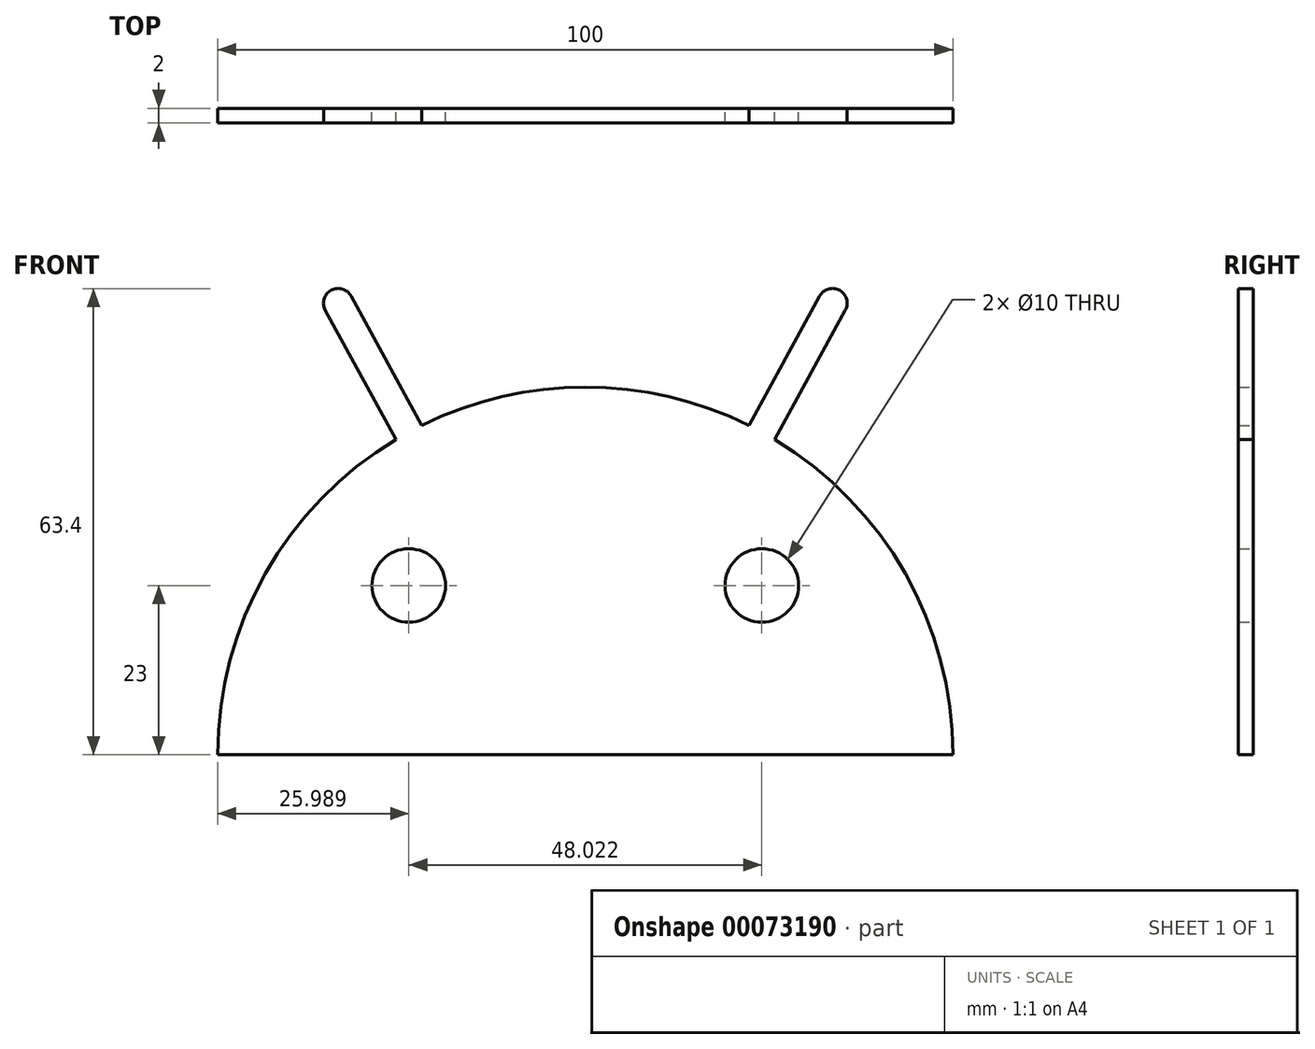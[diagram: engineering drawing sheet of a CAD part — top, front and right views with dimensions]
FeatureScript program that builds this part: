
annotation { "Feature Type Name" : "Feature", "Feature Type Description" : "" }
export const myFeature = defineFeature(function(context is Context, id is Id, definition is map)
    precondition{}
    {
        {
            var Q0;
            Q0=qCreatedBy(makeId("Front.planeOp"),FACE);
            var sketch = newSketch(context, id + "F0", { "sketchPlane" : qUnion([Q0])});
            skLineSegment(sketch, "E0", {"start": v(-50, 0) * mm, "end": v(50, 0) * mm});
            skArc(sketch, "E1", {"start": v(50, 0) * mm, "mid": v(0, 50) * mm, "end": v(-50, 0) * mm});
            skLineSegment(sketch, "E2", {"start": v(0, 0) * mm, "end": v(38.37, 70.1) * mm, "construction": true});
            skPoint(sketch, "E3", {"position": v(24.01, 43.86) * mm});
            skPoint(sketch, "E4", {"position": v(25.75, 42.86) * mm});
            skLineSegment(sketch, "E5", {"start": v(25.75, 42.86) * mm, "end": v(35.37, 60.44) * mm});
            skArc(sketch, "E6", {"start": v(35.37, 60.44) * mm, "mid": v(35.53, 61.96) * mm, "end": v(34.58, 63.15) * mm});
            skLineSegment(sketch, "E7.MirrorCS", {"start": v(22.24, 44.78) * mm, "end": v(31.86, 62.36) * mm});
            skArc(sketch, "E8.MirrorCS", {"start": v(31.86, 62.36) * mm, "mid": v(33.05, 63.32) * mm, "end": v(34.58, 63.15) * mm});
            skLineSegment(sketch, "E9", {"start": v(24.01, 43.86) * mm, "end": v(24.01, 4.14) * mm, "construction": true});
            skCircle(sketch, "E10", {"center": v(24.01, 23) * mm, "radius": 5 * mm});
            skLineSegment(sketch, "E11", {"start": v(0, 0) * mm, "end": v(0, 50) * mm, "construction": true});
            skLineSegment(sketch, "E12.MirrorCS", {"start": v(-25.75, 42.86) * mm, "end": v(-35.37, 60.44) * mm});
            skArc(sketch, "E13.MirrorCS", {"start": v(-35.37, 60.44) * mm, "mid": v(-35.53, 61.96) * mm, "end": v(-34.58, 63.15) * mm});
            skArc(sketch, "E14.MirrorCS", {"start": v(-31.86, 62.36) * mm, "mid": v(-33.05, 63.32) * mm, "end": v(-34.58, 63.15) * mm});
            skLineSegment(sketch, "E15.MirrorCS", {"start": v(-22.24, 44.78) * mm, "end": v(-31.86, 62.36) * mm});
            skCircle(sketch, "E16.MirrorC", {"center": v(-24.01, 23) * mm, "radius": 5 * mm});
            skSolve(sketch);
        }
        {
            var Q0;
            {var subQ1=sQuery(id+"F0.wireOp",EDGE,"E5");Q0=makeQuery(id+"F0.imprint","IMPRINT",FACE,{"disambiguationData":[TD([[makeQuery(id+"F0.imprint","IMPRINT",EDGE,{"derivedFrom":subQ1}),1.0]])]});}
            var Q1;
            {var subQ0=sQuery(id+"F0.wireOp",EDGE,"E12.MirrorCS");Q1=makeQuery(id+"F0.imprint","IMPRINT",FACE,{"disambiguationData":[TD([[makeQuery(id+"F0.imprint","IMPRINT",EDGE,{"derivedFrom":subQ0}),-1.0]])]});}
            var Q2;
            {var subQ4=sQuery(id+"F0.wireOp",EDGE,"E0");Q2=makeQuery(id+"F0.imprint","IMPRINT",FACE,{"disambiguationData":[TD([[makeQuery(id+"F0.imprint","IMPRINT",EDGE,{"derivedFrom":subQ4}),1.0]])]});}
            extrude(context, id + "F1", {"entities" : qUnion([Q0, Q1, Q2]), "depth" : 2 * mm});
        }
    });
